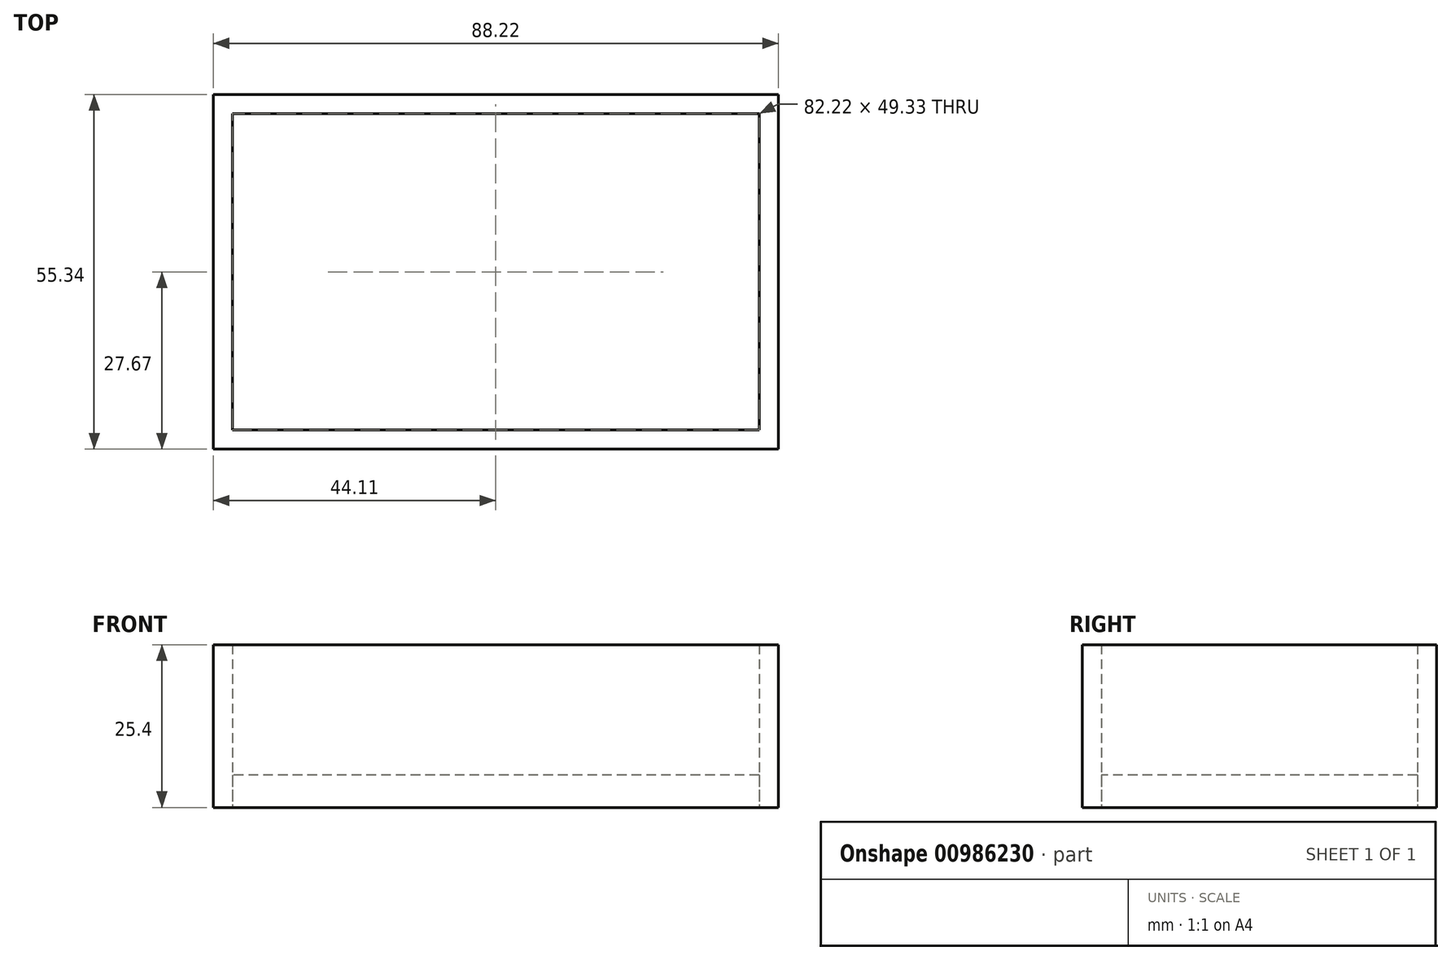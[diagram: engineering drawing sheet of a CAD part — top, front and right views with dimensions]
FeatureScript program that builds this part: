
annotation { "Feature Type Name" : "Feature", "Feature Type Description" : "" }
export const myFeature = defineFeature(function(context is Context, id is Id, definition is map)
    precondition{}
    {
        {
            var Q0;
            Q0=qCreatedBy(makeId("Top.planeOp"),FACE);
            var sketch = newSketch(context, id + "F0", { "sketchPlane" : qUnion([Q0])});
            skLineSegment(sketch, "E0.bottom", {"start": v(41.11, 24.67) * mm, "end": v(-41.11, 24.67) * mm});
            skLineSegment(sketch, "E0.top", {"start": v(41.11, -24.67) * mm, "end": v(-41.11, -24.67) * mm});
            skLineSegment(sketch, "E0.left", {"start": v(41.11, 24.67) * mm, "end": v(41.11, -24.67) * mm});
            skLineSegment(sketch, "E0.right", {"start": v(-41.11, 24.67) * mm, "end": v(-41.11, -24.67) * mm});
            skPoint(sketch, "E0.middle", {"position": v(0, 0) * mm});
            skLineSegment(sketch, "E1.0", {"start": v(44.11, 27.67) * mm, "end": v(44.11, -27.67) * mm});
            skLineSegment(sketch, "E1.1", {"start": v(44.11, 27.67) * mm, "end": v(-44.11, 27.67) * mm});
            skLineSegment(sketch, "E1.2", {"start": v(-44.11, 27.67) * mm, "end": v(-44.11, -27.67) * mm});
            skLineSegment(sketch, "E1.3", {"start": v(44.11, -27.67) * mm, "end": v(-44.11, -27.67) * mm});
            skLineSegment(sketch, "E2.bottom", {"start": v(23.92, 14.48) * mm, "end": v(-23.92, 14.48) * mm, "construction": true});
            skLineSegment(sketch, "E2.top", {"start": v(23.92, -14.48) * mm, "end": v(-23.92, -14.48) * mm, "construction": true});
            skLineSegment(sketch, "E2.left", {"start": v(23.92, 14.48) * mm, "end": v(23.92, -14.48) * mm, "construction": true});
            skLineSegment(sketch, "E2.right", {"start": v(-23.92, 14.48) * mm, "end": v(-23.92, -14.48) * mm, "construction": true});
            skCircle(sketch, "E3", {"center": v(23.92, 14.48) * mm, "radius": 6.7 * mm});
            skCircle(sketch, "E4", {"center": v(-23.92, 14.48) * mm, "radius": 6.7 * mm});
            skCircle(sketch, "E5", {"center": v(-23.92, -14.48) * mm, "radius": 6.7 * mm});
            skCircle(sketch, "E6", {"center": v(23.92, -14.48) * mm, "radius": 6.7 * mm});
            skSolve(sketch);
        }
        {
            var Q0;
            Q0 = qSketchRegion(id + "F0", true);
            var sketch = newSketch(context, id + "F1", { "sketchPlane" : qUnion([Q0])});
            skSolve(sketch);
        }
        {
            var Q0;
            Q0=makeQuery(id+"F0.imprint","IMPRINT",FACE,{"disambiguationData":[TD([[makeQuery(id+"F0.imprint","IMPRINT",EDGE,{"derivedFrom":sQuery(id+"F0.wireOp",EDGE,"E0.bottom")}),-1.0]])]});
            extrude(context, id + "F2", {"entities" : qUnion([Q0]), "depth" : 25.4 * mm, "offsetDistance" : 25.4 * mm});
        }
        {
            var Q0;
            Q0=makeQuery(id+"F1.imprint","IMPRINT",FACE,{"disambiguationData":[TD([[makeQuery(id+"F1.imprint","IMPRINT",EDGE,{"derivedFrom":makeQuery(id+"F0.imprint","IMPRINT",EDGE,{"derivedFrom":sQuery(id+"F0.wireOp",EDGE,"E0.bottom")})}),1.0]])]});
            var Q1;
            Q1=sQuery(id+"F0.wireOp",EDGE,"E0.right");
            var Q2;
            Q2=sQuery(id+"F0.wireOp",EDGE,"E0.bottom");
            var Q3;
            Q3=sQuery(id+"F0.wireOp",EDGE,"E0.top");
            var Q4;
            Q4=sQuery(id+"F0.wireOp",EDGE,"E1.0");
            extrude(context, id + "F3", {"entities" : qUnion([Q0]), "surfaceOperationType" : NewSurfaceOperationType.ADD, "surfaceEntities" : qUnion([Q1, Q2, Q3, Q4]), "depth" : 5.08 * mm, "offsetDistance" : 25.4 * mm});
        }
    });
